# Revit family: Accesories-Teknion-CEAWS-Wall_Mounted_Shelf-Expansion_Casework+-R2023
name_source: partatom
category: Furniture
units: mm (PartAtom-declared; Revit-internal decimal feet)

## family parameters
Always vertical = Yes
Cut with Voids When Loaded = No
Enable Cutting in Views = No
OmniClass Number = 23.40.20.00
OmniClass Title = General Furniture and Specialties
Render Appearance Source = Family Geometry
Room Calculation Point = No
Shared = Yes
Work Plane-Based = No

## types (4) — shared parameters
Assembly Code = E2020200
Depth = 9 "
Description = Wall Mounted Shelf
Height = 56 "
Manufacturer = Teknion
Manufacturer Fax = 416.661.4586
Part Number = CEAWS
Product Documentation Link = http://www.teknion.com
Product Line = Exapnsion Casework +
Product Page URL = https://www.teknion.com
Series = Accesories
Sustainability Data = https://www.teknion.com
URL = www.teknion.com
Unit Weight URL = http://www.teknion.com
Warranty = http://www.teknion.com
zero-valued in all types: Default Elevation

## per-type parameters (varying)
| type | L | Model | R |
| (B) Alignment Holes - Both Sides | Yes | CEAWS_B | Yes |
| (L) Alignment Holes - Left | Yes | CEAWS_L | No |
| (R) Alignment Holes - Right | No | CEAWS_R | Yes |
| (N) No Alignment Holes | No | CEAWS_N | No |

## geometry (parser evidence)
native form markers: Sweep x3
no freeform markers — native parametric forms only
